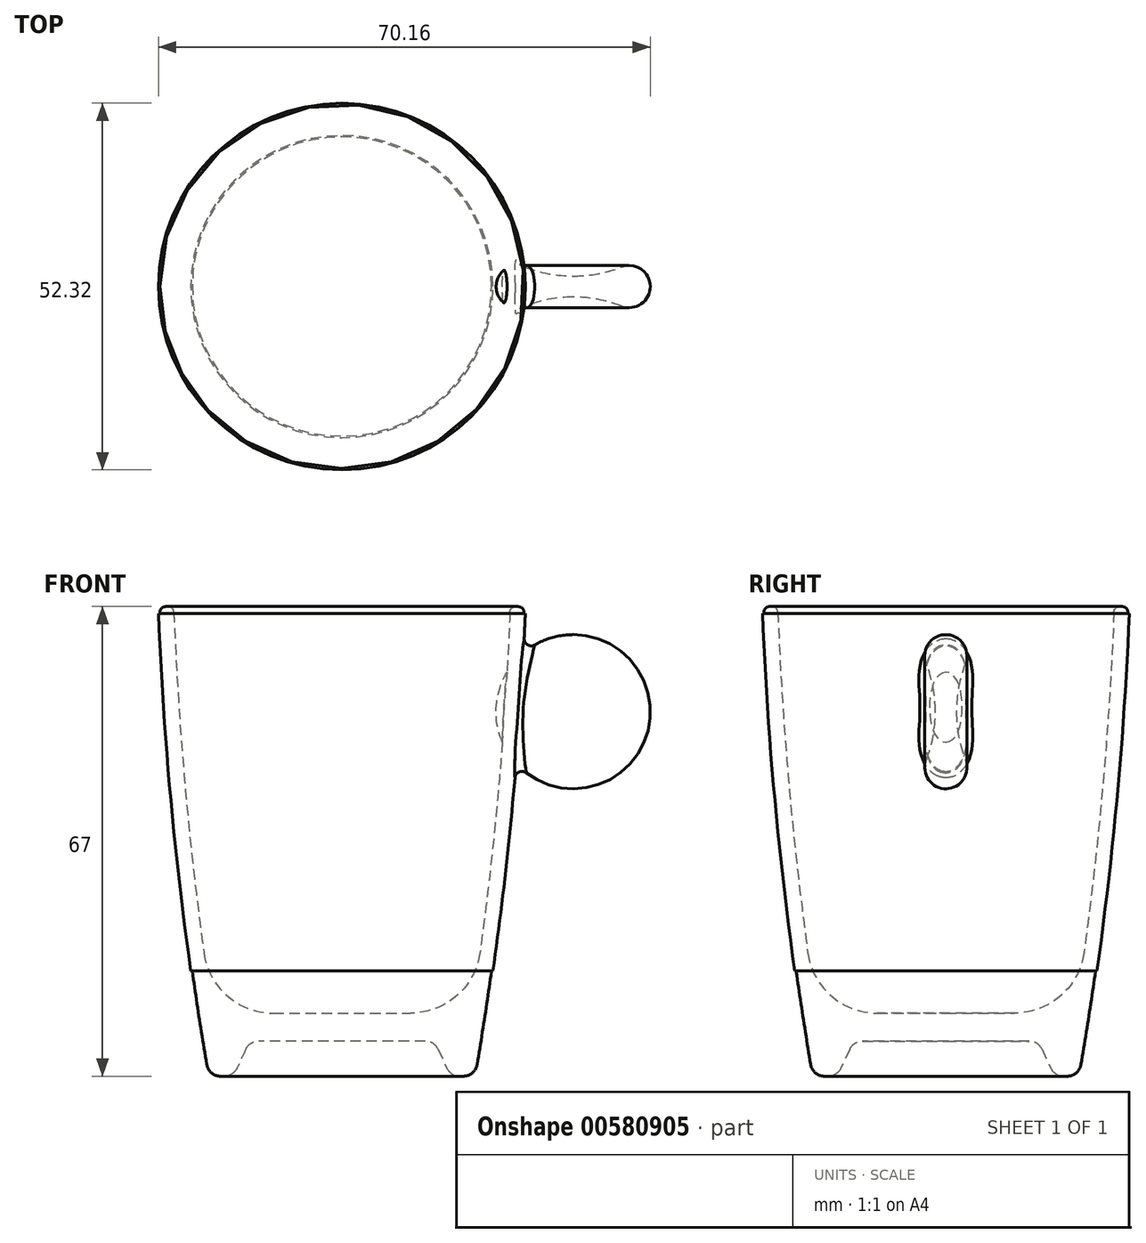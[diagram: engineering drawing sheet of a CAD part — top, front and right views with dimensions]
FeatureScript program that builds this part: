
annotation { "Feature Type Name" : "Feature", "Feature Type Description" : "" }
export const myFeature = defineFeature(function(context is Context, id is Id, definition is map)
    precondition{}
    {
        {
            var Q0;
            Q0=qCreatedBy(makeId("Front.planeOp"),FACE);
            var sketch = newSketch(context, id + "F0", { "sketchPlane" : qUnion([Q0])});
            skLineSegment(sketch, "E0", {"start": v(0, 5) * mm, "end": v(13.17, 5) * mm});
            skLineSegment(sketch, "E1", {"start": v(13.17, 5) * mm, "end": v(15.5, 0) * mm});
            skLineSegment(sketch, "E2", {"start": v(15.5, 0) * mm, "end": v(19, 0) * mm});
            skArc(sketch, "E3", {"start": v(19, 0) * mm, "mid": v(23.6, 33.38) * mm, "end": v(26, 67) * mm});
            skLineSegment(sketch, "E4", {"start": v(26, 67) * mm, "end": v(24, 67) * mm});
            skLineSegment(sketch, "E5", {"start": v(0, 9) * mm, "end": v(0, 5) * mm});
            skLineSegment(sketch, "E6", {"start": v(18.44, 9) * mm, "end": v(0, 9) * mm});
            skArc(sketch, "E7.trimOffspring", {"start": v(18.44, 9) * mm, "mid": v(22.05, 37.92) * mm, "end": v(24, 67) * mm});
            skPoint(sketch, "E8.orphan", {"position": v(0, 67) * mm});
            skSolve(sketch);
        }
        {
            var Q0;
            Q0=qSketchRegion(id+"F0",true);
            var Q1;
            Q1=sQuery(id+"F0.wireOp",EDGE,"E5");
            revolve(context, id + "F1", {"entities" : qUnion([Q0]), "axis" : qUnion([Q1]), "revolveType" : RevolveType.FULL});
        }
        {
            var Q0;
            Q0=makeQuery(id+"F1.opRevolve","SWEPT_EDGE",EDGE,{"disambiguationData":[OSD([sQuery(id+"F0.wireOp",EDGE,"E4"),sQuery(id+"F0.wireOp",EDGE,"E7.trimOffspring")])]});
            var Q1;
            Q1=makeQuery(id+"F1.opRevolve","SWEPT_EDGE",EDGE,{"disambiguationData":[OSD([sQuery(id+"F0.wireOp",EDGE,"E3"),sQuery(id+"F0.wireOp",EDGE,"E4")])]});
            fillet(context, id + "F2", {"entities" : qUnion([Q0, Q1]), "radius" : .8 * mm, "tangentPropagation" : true, "allowEdgeOverflow" : false});
        }
        {
            var Q0;
            Q0=makeQuery(id+"F1.opRevolve","SWEPT_EDGE",EDGE,{"disambiguationData":[OSD([sQuery(id+"F0.wireOp",EDGE,"E2"),sQuery(id+"F0.wireOp",EDGE,"E3")])]});
            var Q1;
            Q1=makeQuery(id+"F1.opRevolve","SWEPT_EDGE",EDGE,{"disambiguationData":[OSD([sQuery(id+"F0.wireOp",EDGE,"E1"),sQuery(id+"F0.wireOp",EDGE,"E2")])]});
            var Q2;
            Q2=makeQuery(id+"F1.opRevolve","SWEPT_EDGE",EDGE,{"disambiguationData":[OSD([sQuery(id+"F0.wireOp",EDGE,"E0"),sQuery(id+"F0.wireOp",EDGE,"E1")])]});
            fillet(context, id + "F3", {"entities" : qUnion([Q0, Q1, Q2]), "radius" : 2 * mm, "tangentPropagation" : true, "allowEdgeOverflow" : false});
        }
        {
            var Q0;
            Q0=makeQuery(id+"F1.opRevolve","SWEPT_EDGE",EDGE,{"disambiguationData":[OSD([sQuery(id+"F0.wireOp",EDGE,"E6"),sQuery(id+"F0.wireOp",EDGE,"E7.trimOffspring")])]});
            fillet(context, id + "F4", {"entities" : qUnion([Q0]), "radius" : 10 * mm, "tangentPropagation" : true, "allowEdgeOverflow" : false});
        }
        {
            var Q0;
            Q0=qCreatedBy(makeId("Front.planeOp"),FACE);
            var sketch = newSketch(context, id + "F5", { "sketchPlane" : qUnion([Q0])});
            skArc(sketch, "E9", {"start": v(21.35, 15) * mm, "mid": v(24.3, 40.44) * mm, "end": v(25.96, 66) * mm});
            skLineSegment(sketch, "E10", {"start": v(25.96, 66) * mm, "end": v(26.16, 66) * mm});
            skLineSegment(sketch, "E11", {"start": v(21.35, 15) * mm, "end": v(21.55, 15) * mm});
            skArc(sketch, "E12", {"start": v(21.55, 15) * mm, "mid": v(24.5, 40.44) * mm, "end": v(26.16, 66) * mm});
            skSolve(sketch);
        }
        {
            var Q0;
            Q0=qSketchRegion(id+"F5",true);
            var Q1;
            Q1=sQuery(id+"F0.wireOp",EDGE,"E5");
            revolve(context, id + "F6", {"operationType" : NewBodyOperationType.ADD, "entities" : qUnion([Q0]), "axis" : qUnion([Q1]), "revolveType" : RevolveType.FULL});
        }
        {
            var Q0;
            Q0=makeQuery(id+"F1.opRevolve","SWEPT_FACE",FACE,{"disambiguationData":[OSD([sQuery(id+"F0.wireOp",EDGE,"E4")])]});
            cPlane(context, id + "F7", {"entities" : qUnion([Q0]), "cplaneType" : CPlaneType.OFFSET, "offset" : 15 * mm, "oppositeDirection" : true, "width" : 150 * mm, "height" : 150 * mm});
        }
        {
            var Q0;
            Q0=qCreatedBy(id+"F7.planeOp",FACE);
            var sketch = newSketch(context, id + "F8", { "sketchPlane" : qUnion([Q0])});
            skArc(sketch, "E13", {"start": v(44, 0) * mm, "mid": v(42.7, 2.48) * mm, "end": v(39.91, 2.8) * mm});
            skArc(sketch, "E14", {"start": v(33, 1.5) * mm, "mid": v(36.52, 1.83) * mm, "end": v(39.91, 2.8) * mm});
            skLineSegment(sketch, "E15", {"start": v(33, 1.5) * mm, "end": v(33, 0) * mm});
            skLineSegment(sketch, "E16.MirrorCS", {"start": v(33, -1.5) * mm, "end": v(33, 0) * mm});
            skArc(sketch, "E17.MirrorCS", {"start": v(33, -1.5) * mm, "mid": v(36.52, -1.83) * mm, "end": v(39.91, -2.8) * mm});
            skArc(sketch, "E18.MirrorCS", {"start": v(44, 0) * mm, "mid": v(42.7, -2.48) * mm, "end": v(39.91, -2.8) * mm});
            skSolve(sketch);
        }
        {
            var Q0;
            Q0=makeQuery(id+"F8.imprint","IMPRINT",FACE,{"disambiguationData":[TD([[makeQuery(id+"F8.imprint","IMPRINT",EDGE,{"derivedFrom":sQuery(id+"F8.wireOp",EDGE,"E13")}),1.0]])]});
            var Q1;
            Q1=sQuery(id+"F8.wireOp",EDGE,"E15");
            revolve(context, id + "F9", {"operationType" : NewBodyOperationType.ADD, "entities" : qUnion([Q0]), "axis" : qUnion([Q1]), "revolveType" : RevolveType.FULL});
        }
        {
            var Q0;
            Q0=makeQuery(id+"F9.boolean.opBoolean","INTERSECT",EDGE,{"derivedFrom":[makeQuery(id+"F6.opRevolve","SWEPT_FACE",FACE,{"disambiguationData":[OSD([sQuery(id+"F5.wireOp",EDGE,"E12")])]}),makeQuery(id+"F9.opRevolve","SWEPT_FACE",FACE,{"disambiguationData":[OSD([sQuery(id+"F8.wireOp",EDGE,"E13"),sQuery(id+"F8.wireOp",EDGE,"E18.MirrorCS")])]})]});
            fillet(context, id + "F10", {"entities" : qUnion([Q0]), "radius" : 1 * mm, "tangentPropagation" : true, "allowEdgeOverflow" : false});
        }
    });
